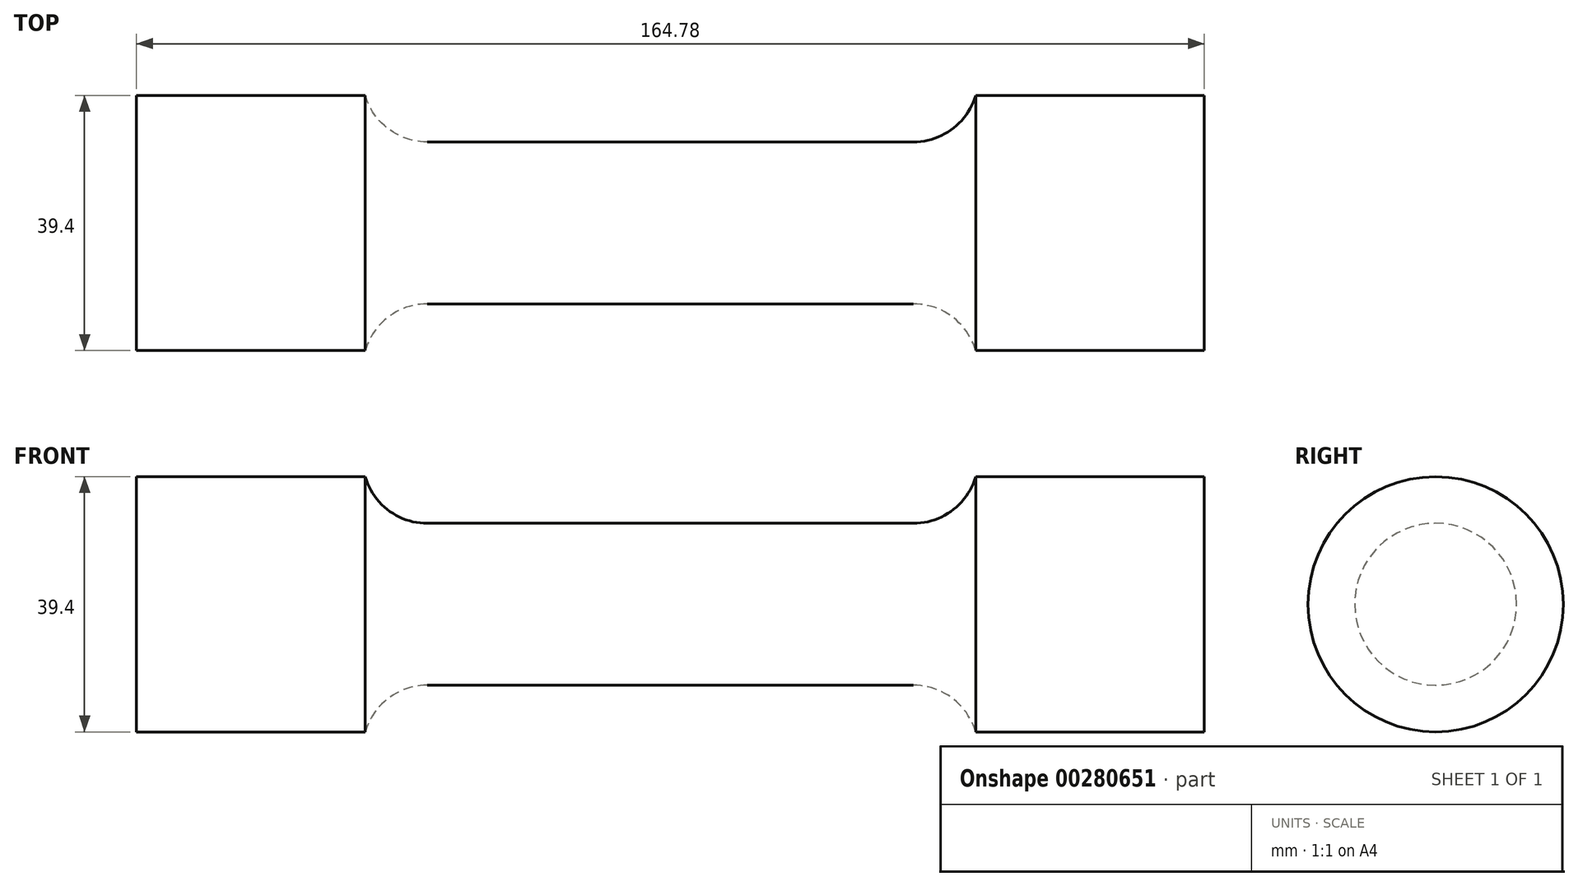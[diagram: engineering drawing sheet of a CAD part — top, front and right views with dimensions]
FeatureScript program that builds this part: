
annotation { "Feature Type Name" : "Feature", "Feature Type Description" : "" }
export const myFeature = defineFeature(function(context is Context, id is Id, definition is map)
    precondition{}
    {
        {
            var Q0;
            Q0=qCreatedBy(makeId("Front.planeOp"),FACE);
            var sketch = newSketch(context, id + "F0", { "sketchPlane" : qUnion([Q0])});
            skLineSegment(sketch, "E0", {"start": v(0, 12.5) * mm, "end": v(37.5, 12.5) * mm});
            skArc(sketch, "E1", {"start": v(37.5, 12.5) * mm, "mid": v(43.5, 14.5) * mm, "end": v(47.1, 19.7) * mm});
            skLineSegment(sketch, "E2", {"start": v(47.1, 19.7) * mm, "end": v(82.4, 19.7) * mm});
            skLineSegment(sketch, "E3", {"start": v(82.4, 19.7) * mm, "end": v(82.4, 0) * mm});
            skLineSegment(sketch, "E4.MirrorCS", {"start": v(0, 12.5) * mm, "end": v(-37.5, 12.5) * mm});
            skLineSegment(sketch, "E5.MirrorCS", {"start": v(-82.4, 19.7) * mm, "end": v(-82.4, 0) * mm});
            skLineSegment(sketch, "E6.MirrorCS", {"start": v(-47.1, 19.7) * mm, "end": v(-82.4, 19.7) * mm});
            skArc(sketch, "E7.MirrorCS", {"start": v(-37.5, 12.5) * mm, "mid": v(-43.5, 14.5) * mm, "end": v(-47.1, 19.7) * mm});
            skLineSegment(sketch, "E8", {"start": v(-82.4, 0) * mm, "end": v(82.4, 0) * mm});
            skSolve(sketch);
        }
        {
            var Q0;
            Q0 = qSketchRegion(id + "F0", true);
            var Q1;
            Q1=sQuery(id+"F0.wireOp",EDGE,"E8");
            revolve(context, id + "F1", {"entities" : qUnion([Q0]), "axis" : qUnion([Q1]), "revolveType" : RevolveType.FULL});
        }
    });
